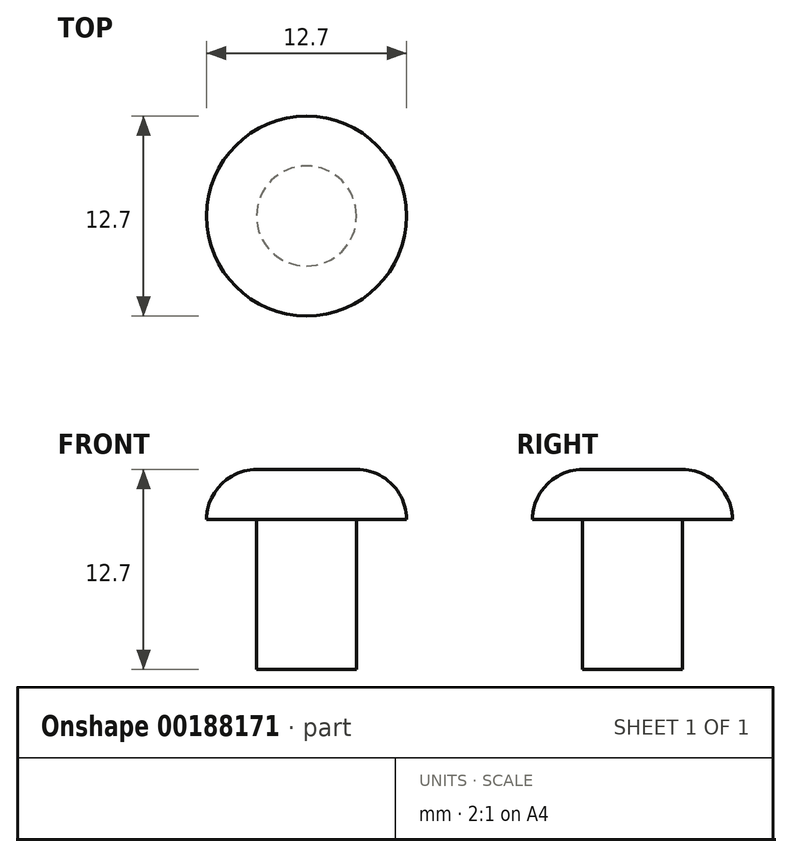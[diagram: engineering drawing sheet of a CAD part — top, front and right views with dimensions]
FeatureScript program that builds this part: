
annotation { "Feature Type Name" : "Feature", "Feature Type Description" : "" }
export const myFeature = defineFeature(function(context is Context, id is Id, definition is map)
    precondition{}
    {
        {
            var Q0;
            Q0=qCreatedBy(makeId("Front.planeOp"),FACE);
            var sketch = newSketch(context, id + "F0", { "sketchPlane" : qUnion([Q0])});
            skLineSegment(sketch, "E0", {"start": v(0, 0) * mm, "end": v(3.18, 0) * mm});
            skLineSegment(sketch, "E1", {"start": v(3.18, 0) * mm, "end": v(3.18, 9.53) * mm});
            skLineSegment(sketch, "E2", {"start": v(3.18, 9.53) * mm, "end": v(6.35, 9.53) * mm});
            skLineSegment(sketch, "E3", {"start": v(0, 0) * mm, "end": v(0, 12.7) * mm});
            skLineSegment(sketch, "E4", {"start": v(0, 12.7) * mm, "end": v(3.18, 12.7) * mm});
            skLineSegment(sketch, "E5", {"start": v(0, 27.15) * mm, "end": v(0, -11.23) * mm, "construction": true});
            skArc(sketch, "E6", {"start": v(6.35, 9.52) * mm, "mid": v(5.42, 11.77) * mm, "end": v(3.18, 12.7) * mm});
            skSolve(sketch);
        }
        {
            var Q0;
            Q0=makeQuery(id+"F0.imprint","IMPRINT",FACE,{"disambiguationData":[TD([[makeQuery(id+"F0.imprint","IMPRINT",EDGE,{"derivedFrom":sQuery(id+"F0.wireOp",EDGE,"E0")}),1.0]])]});
            var Q1;
            Q1=sQuery(id+"F0.wireOp",EDGE,"E5");
            revolve(context, id + "F1", {"entities" : qUnion([Q0]), "axis" : qUnion([Q1]), "revolveType" : RevolveType.FULL});
        }
    });
